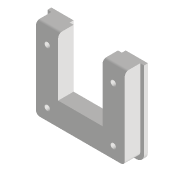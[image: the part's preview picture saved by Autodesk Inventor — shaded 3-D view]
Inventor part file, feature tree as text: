
AUTODESK INVENTOR PART (.ipt)
format: ipt  version: 2022 (Build 260153000, 153)  size: 184,832 bytes
history: native  units: mm
features: sketch x5, extrude x4, projected_geometry x3, fillet x1, hole x1
ambient origin geometry x8: Origin, YZ Plane, XZ Plane, XY Plane, X Axis, Y Axis, Z Axis, Center Point
bodies: Volumenkörper1 (feature_tree)
feature tree (14):
  extrude  "Extrusion1"  Depth=23.0mm
  extrude  "Extrusion2"  Depth=30.0mm
  extrude  "Extrusion3"  Depth=46.0mm
  fillet  "Rundung1"  Radius=10.0mm
  extrude  "Extrusion4"  Depth=25.0mm TaperAngle=0.0deg
  hole  "Bohrung1"  [1 undecoded]
  sketch  "Skizze1"  dims[d0=23.0mm d1=76.0mm]
  sketch  "Skizze2"  dims[d2=12.0mm d3=30.0mm]
  sketch  "Skizze3"  dims[d4=30.0mm d5=46.0mm d6=10.0mm d7=0.0mm]
  projected_geometry  "Projizierte Kontur1"
  sketch  "Skizze4"  dims[d8=0.5mm d9=25.0mm d10=0.0mm]
  projected_geometry  "Projizierte Kontur2"
  sketch  "Skizze5"  dims[d11=3.0mm d12=10.0mm d13=0.0mm d14=2.0mm d15=2.0mm d16=2.0mm d17=0.0mm d18=2.0mm d19=2.0mm d20=0.0mm d21=2.8mm d22=6.0mm d23=4.0mm d24=2.0mm d25=90.0deg d26=12.0mm d27=20.594885mm]
  projected_geometry  "Projizierte Kontur3"
note: 1 required parameter value undecoded (feature->parameter linkage not recoverable at this tier; creation-order binding heuristic only, values carry confidence <= 0.55)
